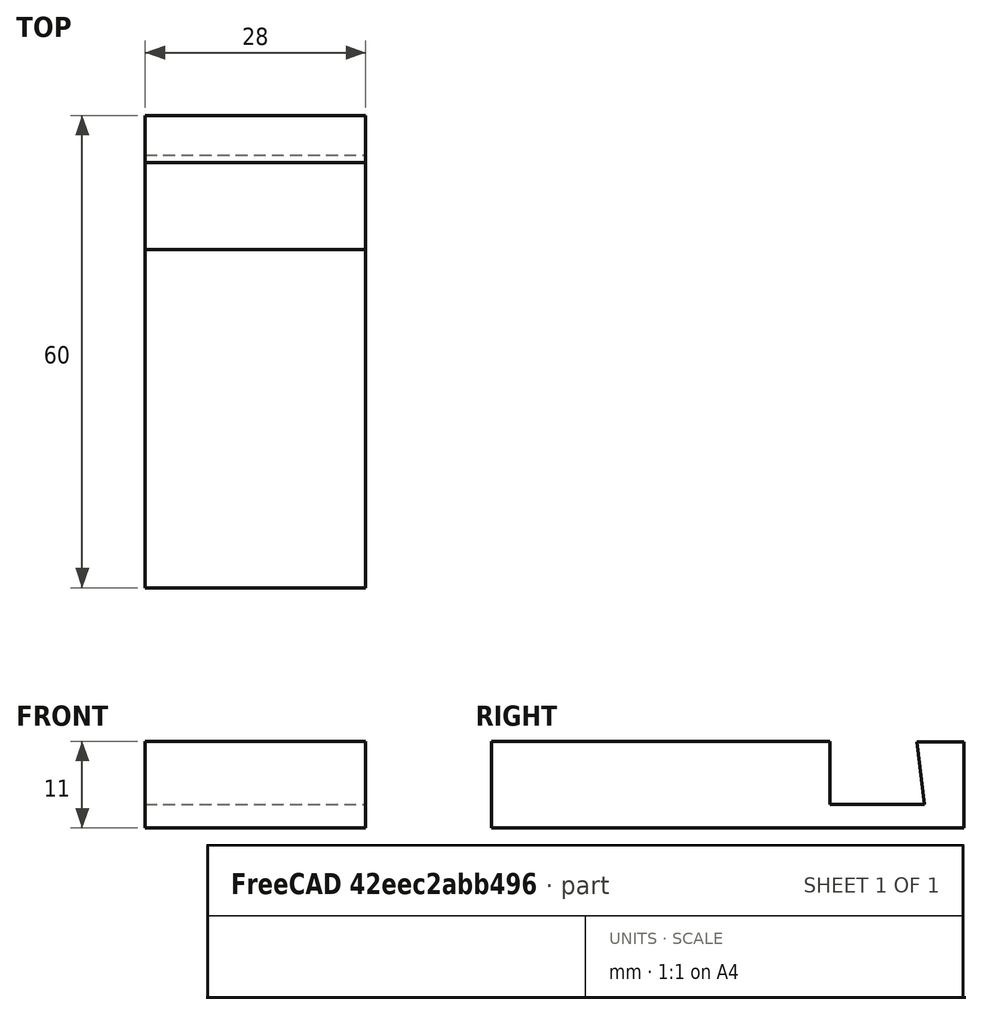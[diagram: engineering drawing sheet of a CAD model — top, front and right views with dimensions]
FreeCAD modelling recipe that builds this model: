
FCSTD DOCUMENT  (FreeCAD 0.21R33694 (Git))
Label: Solución Reto 4
License: All rights reserved
LicenseURL: http://en.wikipedia.org/wiki/All_rights_reserved
objects: Sketcher::SketchObject×1, PartDesign::Pad×1, PartDesign::Body×1
note: 4 computed .brp shape members not serialized (recipe doc carries the construction recipe); baked Part::Feature solids carry a one-line shape summary decoded from their .brp

FEATURE [Sketcher::SketchObject] Sketch
  FullyConstrained = true
  MapMode = 5
  Placement = pos=(0,0,0) rot=(0.57735,0.57735,0.57735;2.0944rad)
  Support = -> [YZ_Plane]
  sketch-geometry (8):
    g0: LineSegment StartX=0 StartY=0 StartZ=0 EndX=0 EndY=11 EndZ=0
    g1: LineSegment StartX=0 StartY=11 StartZ=0 EndX=43.0004 EndY=11 EndZ=0
    g2: LineSegment StartX=43.0004 StartY=11 StartZ=0 EndX=43.0004 EndY=3 EndZ=0
    g3: LineSegment StartX=43.0004 StartY=3 StartZ=0 EndX=55.0004 EndY=3 EndZ=0
    g4: LineSegment StartX=55.0004 StartY=3 StartZ=0 EndX=54 EndY=10.9112 EndZ=0
    g5: LineSegment StartX=54 StartY=10.9112 StartZ=0 EndX=60 EndY=10.9112 EndZ=0
    g6: LineSegment StartX=60 StartY=10.9112 StartZ=0 EndX=60 EndY=0 EndZ=0
    g7: LineSegment StartX=60 StartY=0 StartZ=0 EndX=0 EndY=0 EndZ=0
  constraints (23):
    c: Coincident(g-1,g0)
    c: PointOnObject(g0,g-2)
    c: Coincident(g0,g1)
    c: Horizontal(g1)
    c: Coincident(g1,g2)
    c: Vertical(g2)
    c: Coincident(g2,g3)
    c: Horizontal(g3)
    c: Coincident(g3,g4)
    c: Coincident(g4,g5)
    c: Horizontal(g5)
    c: Coincident(g5,g6)
    c: PointOnObject(g6,g-1)
    c: Vertical(g6)
    c: Coincident(g6,g7)
    c: Coincident(g7,g0)
    c: Distance(g4,g1) = 11
    c: Distance(g3,g7) = 3
    c: DistanceX(g5,g5) = 6
    c: DistanceX(g3,g3) = 12
    c: DistanceY(g0,g0) = 11
    c: DistanceX(g7,g7) = 60
    c: Block(g5)
FEATURE [PartDesign::Pad] Pad
  Direction = (1,-2e-16,3e-16)
  Length = 28
  Length2 = 10
  Placement = pos=(0,0,0) rot=(1,1,1;2.0944rad)
  Profile = -> Sketch
  ReferenceAxis = -> Sketch [N_Axis]
  Refine = true
  Type = 0
FEATURE [PartDesign::Body] Body  label="Cuerpo"
  Group = -> [Sketch,Pad]
  Origin = -> Origin
  Tip = -> Pad
